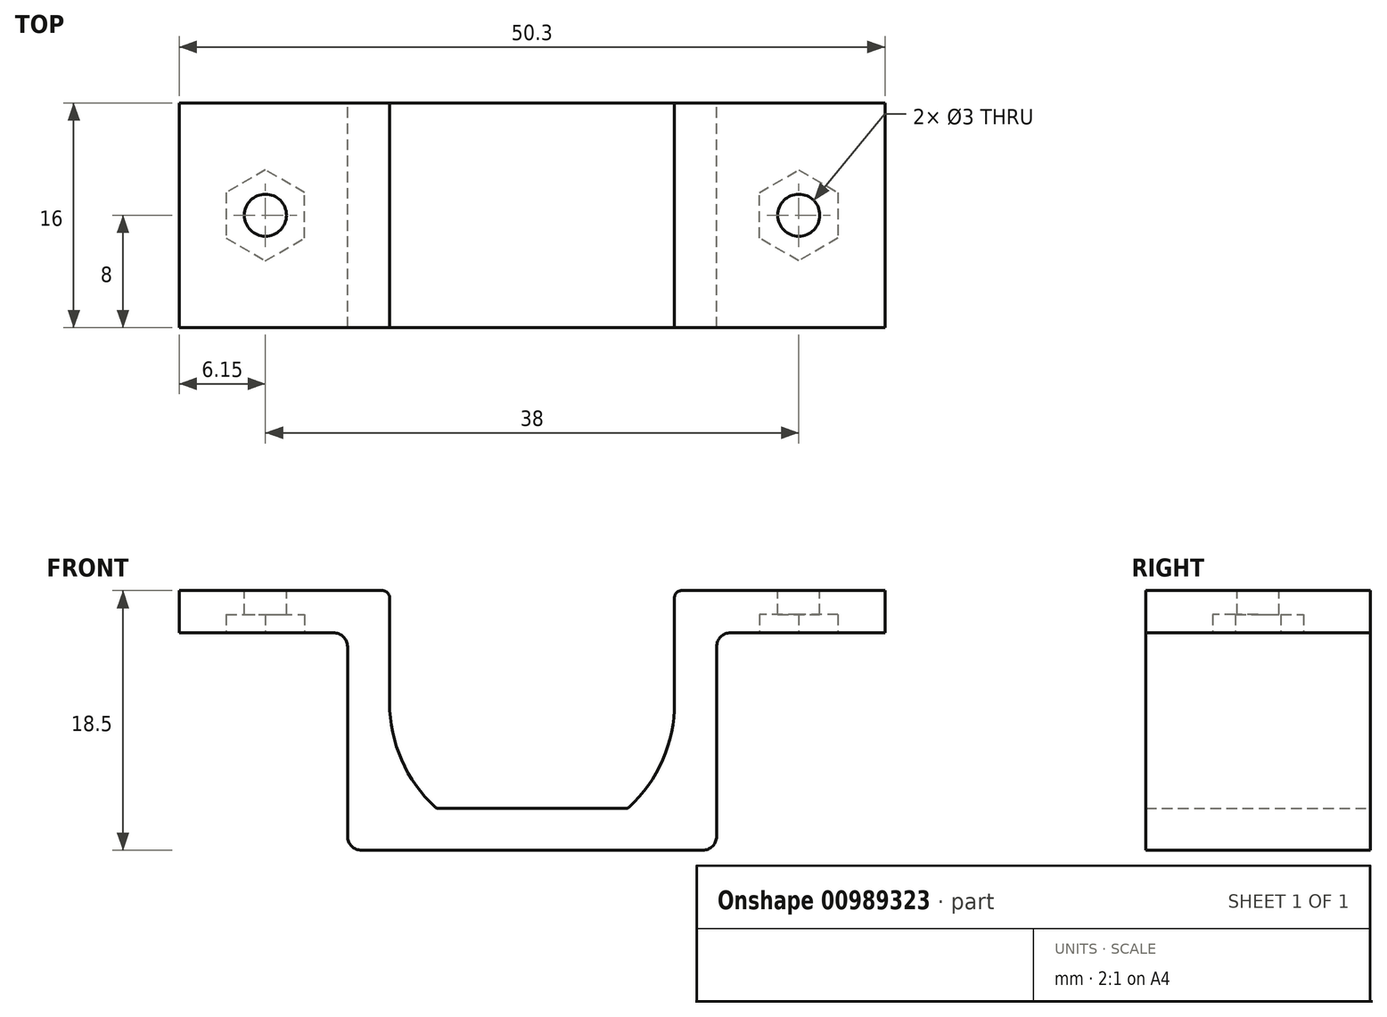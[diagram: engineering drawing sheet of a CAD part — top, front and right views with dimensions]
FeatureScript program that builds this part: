
annotation { "Feature Type Name" : "Feature", "Feature Type Description" : "" }
export const myFeature = defineFeature(function(context is Context, id is Id, definition is map)
    precondition{}
    {
        {
            var Q0;
            Q0=qCreatedBy(makeId("Front.planeOp"),FACE);
            var sketch = newSketch(context, id + "F0", { "sketchPlane" : qUnion([Q0])});
            skLineSegment(sketch, "E0.bottom", {"start": v(-12.15, 0) * mm, "end": v(12.15, 0) * mm});
            skLineSegment(sketch, "E0.top", {"start": v(-13.15, 18.5) * mm, "end": v(-10.15, 18.5) * mm});
            skLineSegment(sketch, "E0.left", {"start": v(-13.15, 1) * mm, "end": v(-13.15, 14.5) * mm});
            skLineSegment(sketch, "E0.right", {"start": v(13.15, 1) * mm, "end": v(13.15, 14.5) * mm});
            skArc(sketch, "E1", {"start": v(6.9, 3.05) * mm, "mid": v(9.3, 6.44) * mm, "end": v(10.15, 10.5) * mm});
            skLineSegment(sketch, "E2", {"start": v(-6.76, 3) * mm, "end": v(6.76, 3) * mm});
            skLineSegment(sketch, "E3", {"start": v(10.15, 10.5) * mm, "end": v(10.15, 18.5) * mm});
            skLineSegment(sketch, "E4.MirrorCS", {"start": v(-10.15, 10.5) * mm, "end": v(-10.15, 18.5) * mm});
            skArc(sketch, "E5.trimOffspring", {"start": v(-10.15, 10.5) * mm, "mid": v(-9.3, 6.44) * mm, "end": v(-6.9, 3.05) * mm});
            skLineSegment(sketch, "E6.trimOffspring", {"start": v(10.15, 18.5) * mm, "end": v(13.15, 18.5) * mm});
            skLineSegment(sketch, "E7.bottom", {"start": v(13.15, 18.5) * mm, "end": v(25.15, 18.5) * mm});
            skLineSegment(sketch, "E7.top", {"start": v(14.15, 15.5) * mm, "end": v(25.15, 15.5) * mm});
            skLineSegment(sketch, "E7.right", {"start": v(25.15, 18.5) * mm, "end": v(25.15, 15.5) * mm});
            skLineSegment(sketch, "E8.MirrorCS", {"start": v(-13.15, 18.5) * mm, "end": v(-25.15, 18.5) * mm});
            skLineSegment(sketch, "E9.MirrorCS", {"start": v(-25.15, 18.5) * mm, "end": v(-25.15, 15.5) * mm});
            skLineSegment(sketch, "E10.MirrorCS", {"start": v(-14.15, 15.5) * mm, "end": v(-25.15, 15.5) * mm});
            skPoint(sketch, "E11.visualSharp", {"position": v(-13.15, 15.5) * mm});
            skArc(sketch, "E11.filletArc", {"start": v(-13.15, 14.5) * mm, "mid": v(-13.44, 15.2) * mm, "end": v(-14.15, 15.5) * mm});
            skPoint(sketch, "E12.visualSharp", {"position": v(13.15, 15.5) * mm});
            skArc(sketch, "E12.filletArc", {"start": v(14.15, 15.5) * mm, "mid": v(13.44, 15.2) * mm, "end": v(13.15, 14.5) * mm});
            skPoint(sketch, "E13.visualSharp", {"position": v(-13.15, 0) * mm});
            skArc(sketch, "E13.filletArc", {"start": v(-13.15, 1) * mm, "mid": v(-12.86, 0.3) * mm, "end": v(-12.15, 0) * mm});
            skPoint(sketch, "E14.visualSharp", {"position": v(13.15, 0) * mm});
            skArc(sketch, "E14.filletArc", {"start": v(12.15, 0) * mm, "mid": v(12.86, 0.3) * mm, "end": v(13.15, 1) * mm});
            skPoint(sketch, "E15.visualSharp", {"position": v(-6.84, 3) * mm});
            skArc(sketch, "E15.filletArc", {"start": v(-6.9, 3.05) * mm, "mid": v(-6.83, 3.01) * mm, "end": v(-6.76, 3) * mm});
            skPoint(sketch, "E16.visualSharp", {"position": v(6.84, 3) * mm});
            skArc(sketch, "E16.filletArc", {"start": v(6.76, 3) * mm, "mid": v(6.83, 3.01) * mm, "end": v(6.9, 3.05) * mm});
            skSolve(sketch);
        }
        {
            var Q0;
            Q0=qSketchRegion(id+"F0",true);
            extrude(context, id + "F1", {"entities" : qUnion([Q0]), "depth" : 16 * mm, "offsetDistance" : 25 * mm});
        }
        {
            var Q0;
            Q0=makeQuery(id+"F1.opExtrude","SWEPT_FACE",FACE,{"disambiguationData":[OSD([sQuery(id+"F0.wireOp",EDGE,"E0.top"),sQuery(id+"F0.wireOp",EDGE,"E8.MirrorCS")])]});
            var sketch = newSketch(context, id + "F2", { "sketchPlane" : qUnion([Q0])});
            skCircle(sketch, "E17", {"center": v(-19, -8) * mm, "radius": 1.5 * mm});
            skCircle(sketch, "E18.MirrorC", {"center": v(19, -8) * mm, "radius": 1.5 * mm});
            skSolve(sketch);
        }
        {
            var Q0;
            Q0=qSketchRegion(id+"F2",true);
            extrude(context, id + "F3", {"entities" : qUnion([Q0]), "operationType" : NewBodyOperationType.REMOVE, "endBound" : BoundingType.THROUGH_ALL, "oppositeDirection" : true, "depth" : 25 * mm, "offsetDistance" : 25 * mm});
        }
        {
            var Q0;
            Q0=makeQuery(id+"F1.opExtrude","SWEPT_FACE",FACE,{"disambiguationData":[OSD([sQuery(id+"F0.wireOp",EDGE,"E10.MirrorCS")])]});
            var sketch = newSketch(context, id + "F4", { "sketchPlane" : qUnion([Q0])});
            skCircle(sketch, "E19.cCircle", {"center": v(-19, 8) * mm, "radius": 3.23 * mm, "construction": true});
            skLineSegment(sketch, "E19.0", {"start": v(-16.2, 9.62) * mm, "end": v(-16.2, 6.38) * mm});
            skLineSegment(sketch, "E19.1", {"start": v(-16.2, 6.38) * mm, "end": v(-19, 4.77) * mm});
            skLineSegment(sketch, "E19.2", {"start": v(-19, 4.77) * mm, "end": v(-21.8, 6.38) * mm});
            skLineSegment(sketch, "E19.3", {"start": v(-21.8, 6.38) * mm, "end": v(-21.8, 9.62) * mm});
            skLineSegment(sketch, "E19.4", {"start": v(-21.8, 9.62) * mm, "end": v(-19, 11.23) * mm});
            skLineSegment(sketch, "E19.5", {"start": v(-19, 11.23) * mm, "end": v(-16.2, 9.62) * mm});
            skCircle(sketch, "E20.MirrorC", {"center": v(19, 8) * mm, "radius": 3.23 * mm, "construction": true});
            skLineSegment(sketch, "E21.MirrorCS", {"start": v(16.2, 9.62) * mm, "end": v(16.2, 6.38) * mm});
            skLineSegment(sketch, "E22.MirrorCS", {"start": v(21.8, 9.62) * mm, "end": v(19, 11.23) * mm});
            skLineSegment(sketch, "E23.MirrorCS", {"start": v(19, 11.23) * mm, "end": v(16.2, 9.62) * mm});
            skLineSegment(sketch, "E24.MirrorCS", {"start": v(16.2, 6.38) * mm, "end": v(19, 4.77) * mm});
            skLineSegment(sketch, "E25.MirrorCS", {"start": v(19, 4.77) * mm, "end": v(21.8, 6.38) * mm});
            skLineSegment(sketch, "E26.MirrorCS", {"start": v(21.8, 6.38) * mm, "end": v(21.8, 9.62) * mm});
            skSolve(sketch);
        }
        {
            var Q0;
            Q0=qSketchRegion(id+"F4",true);
            extrude(context, id + "F5", {"entities" : qUnion([Q0]), "operationType" : NewBodyOperationType.REMOVE, "oppositeDirection" : true, "depth" : 1.3 * mm, "offsetDistance" : 25 * mm});
        }
        {
            var Q0;
            Q0=makeQuery(id+"F1.opExtrude","SWEPT_EDGE",EDGE,{"disambiguationData":[OSD([sQuery(id+"F0.wireOp",EDGE,"E0.top"),sQuery(id+"F0.wireOp",EDGE,"E4.MirrorCS")])]});
            var Q1;
            Q1=makeQuery(id+"F1.opExtrude","SWEPT_EDGE",EDGE,{"disambiguationData":[OSD([sQuery(id+"F0.wireOp",EDGE,"E3"),sQuery(id+"F0.wireOp",EDGE,"E6.trimOffspring")])]});
            fillet(context, id + "F6", {"entities" : qUnion([Q0, Q1]), "radius" : 0.5 * mm, "tangentPropagation" : true, "allowEdgeOverflow" : false});
        }
    });
